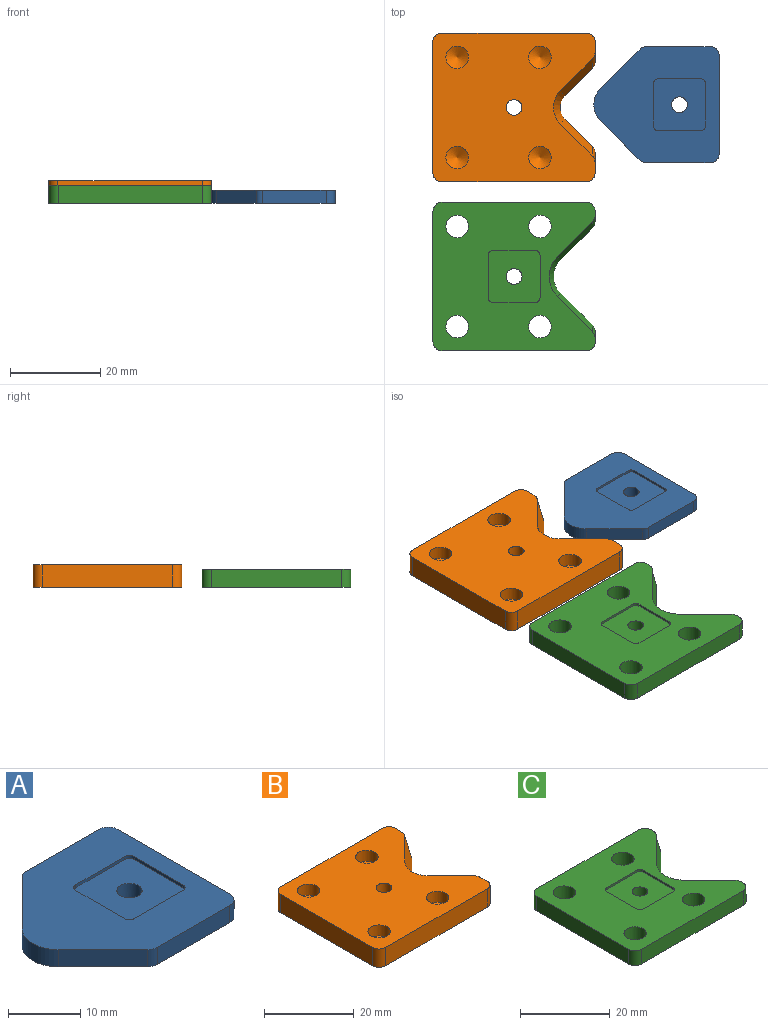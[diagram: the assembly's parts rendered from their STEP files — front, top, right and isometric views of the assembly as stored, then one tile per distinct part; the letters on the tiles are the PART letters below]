
ASSEMBLY  parts=3 mates=2
PART A: 22 faces, bbox 27.8x25.8x2.9 mm
  f0: plane 9.5x0.5mm, normal (1,0,0), area 4.8mm2, adj f10,f12,f18,f21
  f1: plane 9.5x0.5mm, normal (0,-1,0), area 4.8mm2, adj f10,f12,f18,f19
  f2: plane 9.5x0.5mm, normal (-1,0,0), area 4.8mm2, adj f10,f12,f19,f20
  f3: plane 8.78x8.78mm, normal (-0.71,-0.71,0), area 36mm2, adj f8,f10,f11,f14
  f4: plane 14.13x2.9mm, normal (0,-1,0), area 41mm2, adj f10,f11,f14,f15
  f5: plane 21.8x2.9mm, normal (1,0,0), area 63.2mm2, adj f10,f11,f15,f16
  f6: plane 14.13x2.9mm, normal (0,1,0), area 41mm2, adj f10,f11,f16,f17
  f7: plane 8.78x8.78mm, normal (-0.71,0.71,0), area 36mm2, adj f8,f10,f11,f17
  f8: cylinder r=5mm len=7.07mm, axis (0,0,-1), area 22.8mm2, adj f3,f7,f10,f11
  f9: plane 9.5x0.5mm, normal (0,1,0), area 4.8mm2, adj f10,f12,f20,f21
  f10: plane 27.78x25.8mm, normal (0,0,1), area 465.1mm2, adj f0,f1,f2,f3,f4,f5,f6,f7
  f11: plane 27.78x25.8mm, normal (0,0,-1), area 586.9mm2, adj f3,f4,f5,f6,f7,f8,f13,f14
  f12: plane 11.5x11.5mm, normal (0,0,1), area 121.8mm2, adj f0,f1,f2,f9,f13,f18,f19,f20
  f13: cylinder r=1.75mm len=3.5mm, axis (0,0,-1), area 26.4mm2, adj f11,f12
  f14: cylinder r=2mm len=2.9mm, axis (0,0,1), area 4.6mm2, adj f3,f4,f10,f11
  f15: cylinder r=2mm len=2.9mm, axis (0,0,-1), area 9.1mm2, adj f4,f5,f10,f11
  f16: cylinder r=2mm len=2.9mm, axis (0,0,-1), area 9.1mm2, adj f5,f6,f10,f11
  f17: cylinder r=2mm len=2.9mm, axis (0,0,1), area 4.6mm2, adj f6,f7,f10,f11
  f18: cylinder r=1mm len=1mm, axis (0,0,-1), area 0.8mm2, adj f0,f1,f10,f12
  f19: cylinder r=1mm len=1mm, axis (0,0,1), area 0.8mm2, adj f1,f2,f10,f12
  f20: cylinder r=1mm len=1mm, axis (0,0,-1), area 0.8mm2, adj f2,f9,f10,f12
  f21: cylinder r=1mm len=1mm, axis (0,0,1), area 0.8mm2, adj f0,f9,f10,f12
PART B: 25 faces, bbox 36x33x6.1 mm
  f0: cylinder r=1.75mm len=5mm, axis (0,0,-1), area 55mm2, adj f1,f16
  f1: plane 36x33mm, normal (0,0,-1), area 1090.9mm2, adj f0,f2,f3,f4,f5,f6,f7,f8
  f2: cylinder r=2mm len=6.15mm, axis (0,-0.39,-0.92), area 9mm2, adj f1,f13,f14,f16
  f3: cylinder r=2mm len=5mm, axis (0,0,-1), area 15.7mm2, adj f1,f12,f13,f16
  f4: cylinder r=2mm len=5mm, axis (0,0,1), area 15.7mm2, adj f1,f7,f9,f16
  f5: cylinder r=2mm len=6.15mm, axis (0,0.39,-0.92), area 9mm2, adj f1,f6,f7,f16
  f6: plane 8.13x7.07mm, normal (0.68,0.68,0.29), area 48.3mm2, adj f1,f5,f15,f16
  f7: plane 5x4.23mm, normal (1,0,0), area 15.8mm2, adj f1,f4,f5,f16
  f8: cylinder r=2mm len=5mm, axis (0,0,-1), area 15.7mm2, adj f1,f9,f11,f16
  f9: plane 32x5mm, normal (0,-1,0), area 160mm2, adj f1,f4,f8,f16
  f10: cylinder r=2mm len=5mm, axis (0,0,1), area 15.7mm2, adj f1,f11,f12,f16
  f11: plane 29x5mm, normal (-1,0,0), area 145mm2, adj f1,f8,f10,f16
  f12: plane 32x5mm, normal (0,1,0), area 160mm2, adj f1,f3,f10,f16
  f13: plane 5x4.23mm, normal (1,0,0), area 15.8mm2, adj f1,f2,f3,f16
  f14: plane 8.13x7.07mm, normal (0.68,-0.68,0.29), area 48.3mm2, adj f1,f2,f15,f16
  f15: cone r=6.25mm half-angle=16.7deg, axis (0,0,1), area 37mm2, adj f1,f6,f14,f16
  f16: plane 36x33mm, normal (0,0,1), area 971.3mm2, adj f0,f2,f3,f4,f5,f6,f7,f8
  f17: cone r=0mm half-angle=59deg, axis (0,0,1), area 22.9mm2, adj f18
  f18: cylinder r=2.5mm len=5mm, axis (0,0,1), area 47.1mm2, adj f16,f17
  f19: cone r=0mm half-angle=59deg, axis (0,0,1), area 22.9mm2, adj f20
  f20: cylinder r=2.5mm len=5mm, axis (0,0,1), area 47.1mm2, adj f16,f19
  f21: cone r=0mm half-angle=59deg, axis (0,0,1), area 22.9mm2, adj f22
  f22: cylinder r=2.5mm len=5mm, axis (0,0,1), area 47.1mm2, adj f16,f21
  f23: cone r=0mm half-angle=59deg, axis (0,0,1), area 22.9mm2, adj f24
  f24: cylinder r=2.5mm len=5mm, axis (0,0,1), area 47.1mm2, adj f16,f23
PART C: 35 faces, bbox 36x33x4.6 mm
  f0: cylinder r=1mm len=1mm, axis (0,0,-1), area 0.8mm2, adj f4,f5,f28,f29
  f1: cylinder r=1mm len=1mm, axis (0,0,1), area 0.8mm2, adj f5,f6,f28,f29
  f2: cylinder r=1mm len=1mm, axis (0,0,-1), area 0.8mm2, adj f6,f15,f28,f29
  f3: cylinder r=1mm len=1mm, axis (0,0,1), area 0.8mm2, adj f4,f15,f28,f29
  f4: plane 9.5x0.5mm, normal (1,0,0), area 4.7mm2, adj f0,f3,f28,f29
  f5: plane 9.5x0.5mm, normal (0,-1,0), area 4.7mm2, adj f0,f1,f28,f29
  f6: plane 9.5x0.5mm, normal (-1,0,0), area 4.7mm2, adj f1,f2,f28,f29
  f7: cone r=6.25mm half-angle=16.7deg, axis (0,0,1), area 31.1mm2, adj f8,f14,f27,f30
  f8: plane 8.47x7.77mm, normal (0.68,-0.68,0.29), area 36.2mm2, adj f7,f17,f23,f30
  f9: plane 4x2.11mm, normal (1,0,0), area 5.1mm2, adj f17,f18,f24,f28,f30
  f10: plane 32x4mm, normal (0,1,0), area 128mm2, adj f18,f19,f28,f30
  f11: plane 29x4mm, normal (-1,0,0), area 116mm2, adj f19,f20,f28,f30
  f12: plane 32x4mm, normal (0,-1,0), area 128mm2, adj f20,f21,f28,f30
  f13: plane 4x2.11mm, normal (1,0,0), area 5.1mm2, adj f21,f22,f25,f28,f30
  f14: plane 8.47x7.77mm, normal (0.68,0.68,0.29), area 36.2mm2, adj f7,f22,f26,f30
  f15: plane 9.5x0.5mm, normal (0,1,0), area 4.7mm2, adj f2,f3,f28,f29
  f16: cylinder r=1.75mm len=3.5mm, axis (0,0,-1), area 38.5mm2, adj f29,f30
  f17: cylinder r=2mm len=4.45mm, axis (0,-0.39,-0.92), area 5.9mm2, adj f8,f9,f24,f30
  f18: cylinder r=2mm len=4mm, axis (0,0,-1), area 12.6mm2, adj f9,f10,f28,f30
  f19: cylinder r=2mm len=4mm, axis (0,0,1), area 12.6mm2, adj f10,f11,f28,f30
  f20: cylinder r=2mm len=4mm, axis (0,0,-1), area 12.6mm2, adj f11,f12,f28,f30
  f21: cylinder r=2mm len=4mm, axis (0,0,1), area 12.6mm2, adj f12,f13,f28,f30
  f22: cylinder r=2mm len=4.45mm, axis (0,0.39,-0.92), area 5.9mm2, adj f13,f14,f25,f30
  f23: plane 7.77x7.77mm, normal (0.71,-0.71,0), area 7.7mm2, adj f8,f24,f27,f28
  f24: extruded ~1.6x0.7mm, area 1.2mm2, adj f9,f17,f23,f28
  f25: extruded ~1.6x0.7mm, area 1.2mm2, adj f13,f22,f26,f28
  f26: plane 7.77x7.77mm, normal (0.71,0.71,0), area 7.7mm2, adj f14,f25,f27,f28
  f27: cylinder r=6.25mm len=8.84mm, axis (0,0,-1), area 6.9mm2, adj f7,f23,f26,f28
  f28: plane 36x33mm, normal (0,0,1), area 818mm2, adj f0,f1,f2,f3,f4,f5,f6,f9
  f29: plane 11.5x11.5mm, normal (0,0,1), area 121.8mm2, adj f0,f1,f2,f3,f4,f5,f6,f15
  f30: plane 36x33mm, normal (0,0,-1), area 971.3mm2, adj f7,f8,f9,f10,f11,f12,f13,f14
  f31: cylinder r=2.5mm len=5mm, axis (0,0,1), area 62.8mm2, adj f28,f30
  f32: cylinder r=2.5mm len=5mm, axis (0,0,1), area 62.8mm2, adj f28,f30
  f33: cylinder r=2.5mm len=5mm, axis (0,0,1), area 62.8mm2, adj f28,f30
  f34: cylinder r=2.5mm len=5mm, axis (0,0,1), area 62.8mm2, adj f28,f30
PLACE A t=(74.13,41.7,-43.98)mm
PLACE B t=(-34.58,41.03,-35.68)mm
PLACE C t=(-34.56,3.51,-40.68)mm
MATE planar C.f30 <-> B.f1  axis (0,0,-1) through (63.85,3.51,-35.68)mm
MATE planar A.f11 <-> B.f1  axis (0,0,-1) through (98.98,41.64,-35.68)mm
